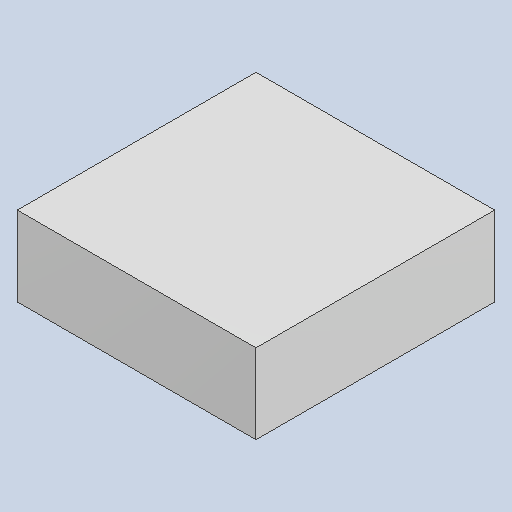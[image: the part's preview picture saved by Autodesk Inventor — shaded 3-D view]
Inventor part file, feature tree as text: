
AUTODESK INVENTOR PART (.ipt)
format: ipt  version: 2023.4 (Build 274418000, 418)  size: 79,872 bytes
history: native  units: mm
features: extrude x1
ambient origin geometry x8: Origin, YZ Plane, XZ Plane, XY Plane, X Axis, Y Axis, Z Axis, Center Point
bodies: Solid1 (feature_tree)
feature tree (1):
  extrude  "Extruded_19"  [1 undecoded]
note: 1 required parameter value undecoded (feature->parameter linkage not recoverable at this tier; creation-order binding heuristic only, values carry confidence <= 0.55)
